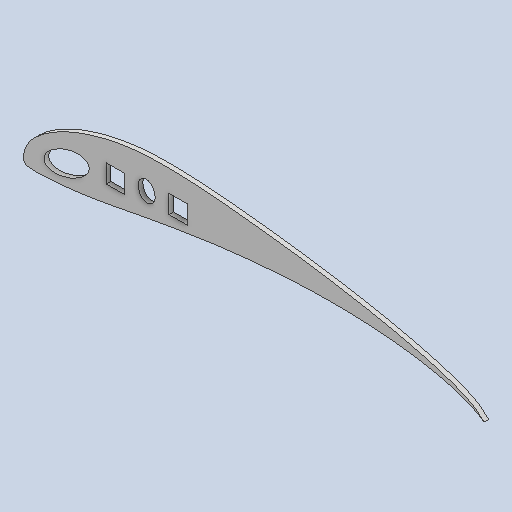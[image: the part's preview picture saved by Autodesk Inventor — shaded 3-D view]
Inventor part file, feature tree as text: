
AUTODESK INVENTOR PART (.ipt)
format: ipt  version: 2024 (Build 280153000, 153)  size: 280,064 bytes
history: native  units: mm
features: extrude x1, sketch x1
ambient origin geometry x8: Origin, YZ Plane, XZ Plane, XY Plane, X Axis, Y Axis, Z Axis, Center Point
bodies: Solid1 (feature_tree)
feature tree (2):
  extrude  "Extrusion1"  [1 undecoded]
  sketch  "Sketch1"  dims[d0=2.5mm d1=0.0mm]
note: 1 required parameter value undecoded (feature->parameter linkage not recoverable at this tier; creation-order binding heuristic only, values carry confidence <= 0.55)
